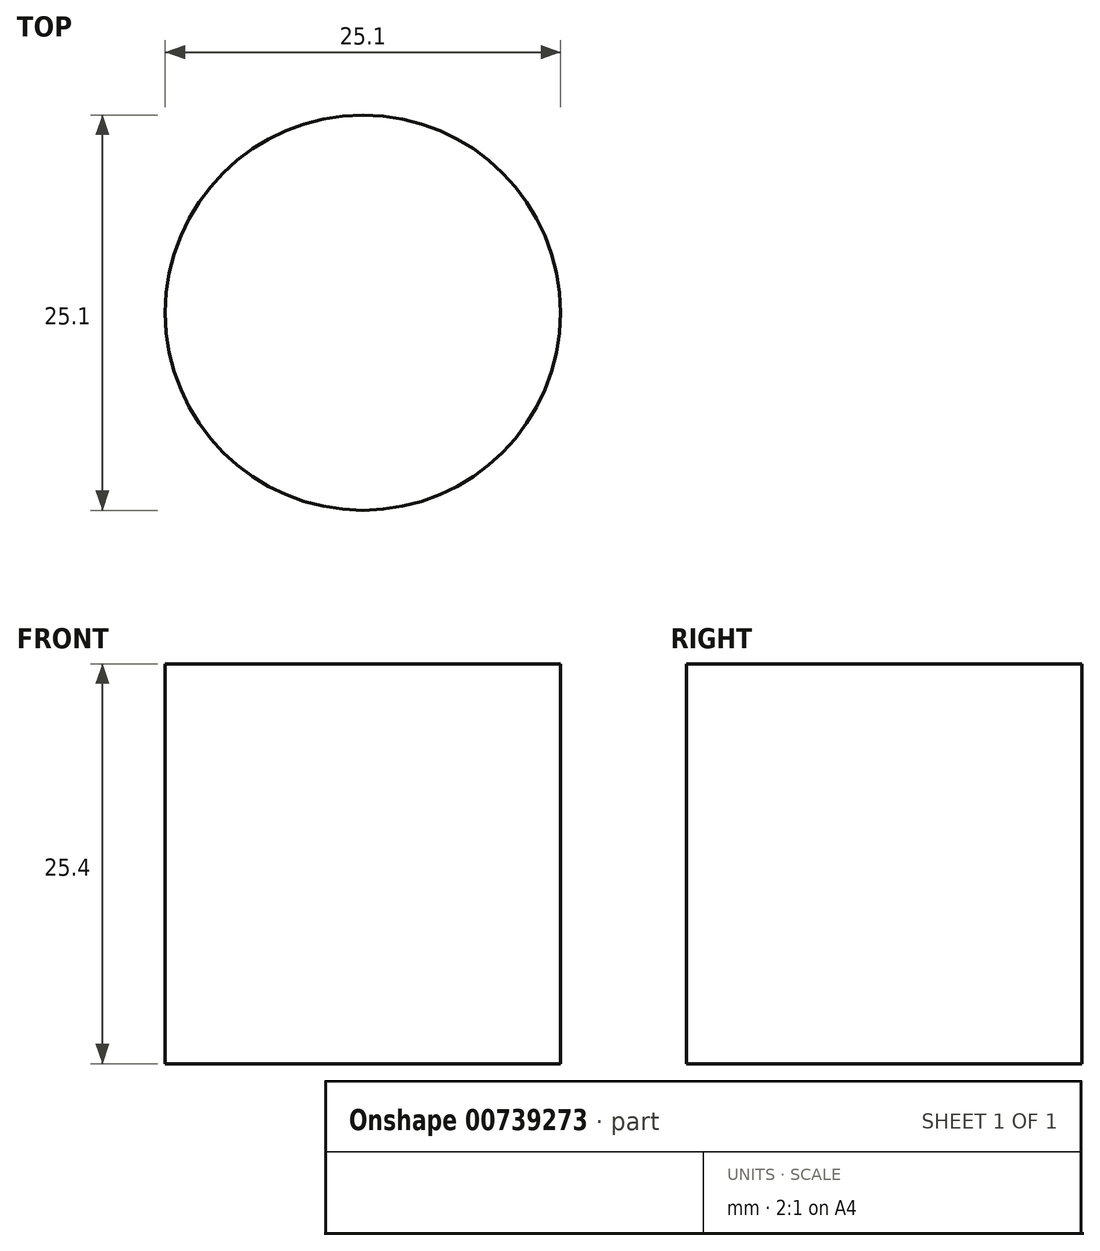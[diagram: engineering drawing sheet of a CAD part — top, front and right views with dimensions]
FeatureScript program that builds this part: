
annotation { "Feature Type Name" : "Feature", "Feature Type Description" : "" }
export const myFeature = defineFeature(function(context is Context, id is Id, definition is map)
    precondition{}
    {
        {
            var Q0;
            Q0=qCreatedBy(makeId("Top.planeOp"),FACE);
            var sketch = newSketch(context, id + "F0", { "sketchPlane" : qUnion([Q0])});
            skCircle(sketch, "E0", {"center": v(0, 0) * mm, "radius": 12.55 * mm});
            skSolve(sketch);
        }
        {
            var Q0;
            Q0 = qSketchRegion(id + "F0", true);
            extrude(context, id + "F1", {"entities" : qUnion([Q0]), "depth" : 25.4 * mm, "offsetDistance" : 25.4 * mm});
        }
    });
